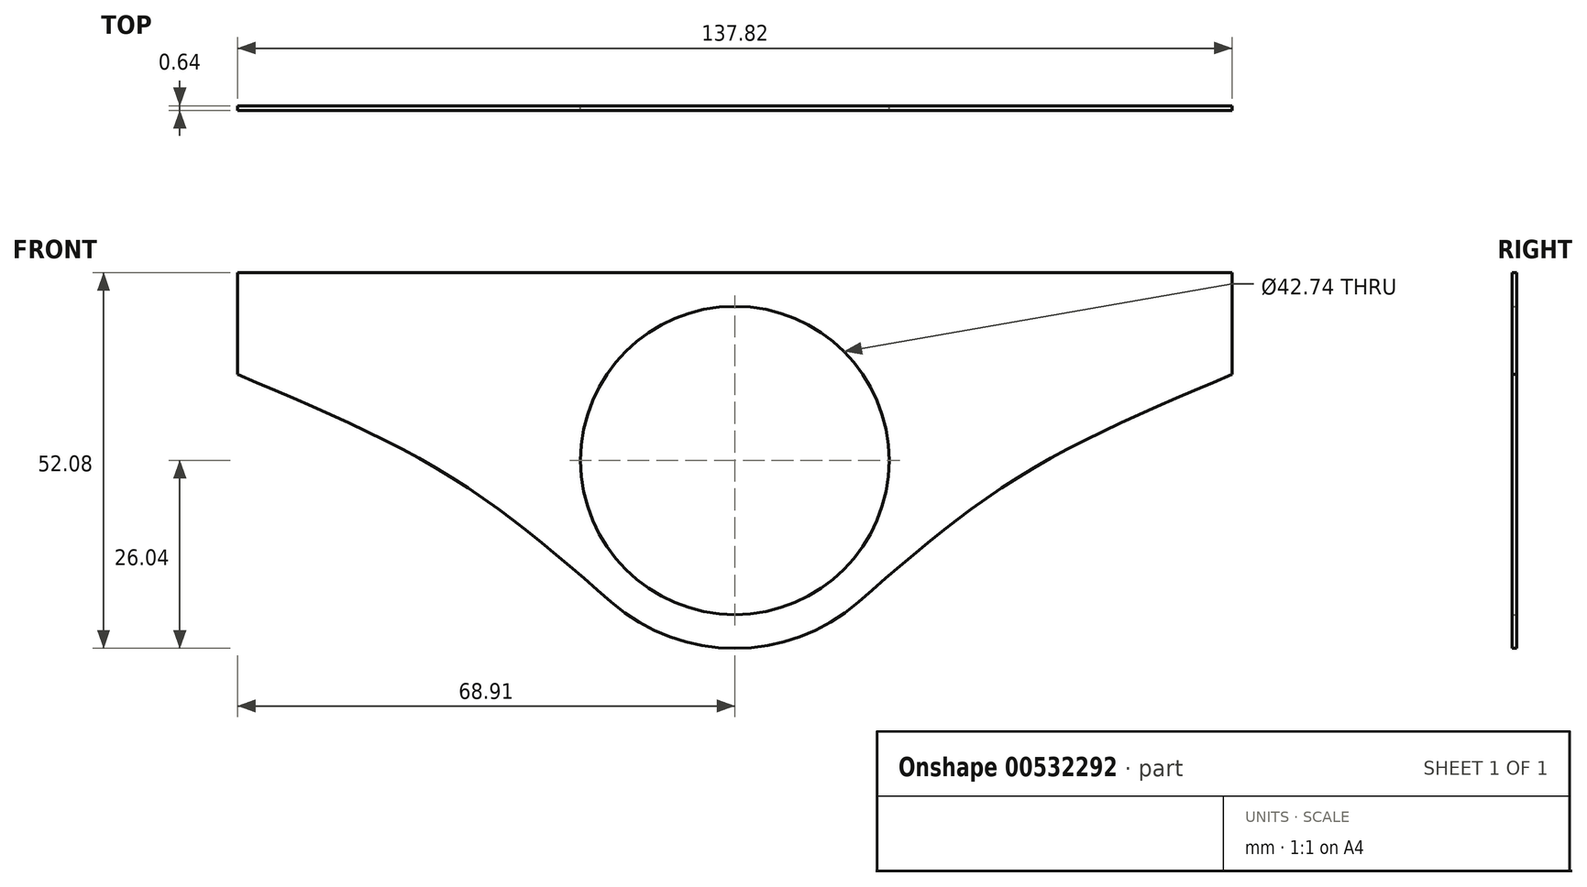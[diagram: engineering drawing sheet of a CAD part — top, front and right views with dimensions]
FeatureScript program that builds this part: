
annotation { "Feature Type Name" : "Feature", "Feature Type Description" : "" }
export const myFeature = defineFeature(function(context is Context, id is Id, definition is map)
    precondition{}
    {
        {
            var Q0;
            Q0=qCreatedBy(makeId("Front.planeOp"),FACE);
            var sketch = newSketch(context, id + "F0", { "sketchPlane" : qUnion([Q0])});
            skCircle(sketch, "E0", {"center": v(0, 0) * mm, "radius": 21.37 * mm});
            skLineSegment(sketch, "E1", {"start": v(0, 26.04) * mm, "end": v(-68.91, 26.04) * mm});
            skLineSegment(sketch, "E2", {"start": v(-68.91, 26.04) * mm, "end": v(-68.91, 11.93) * mm});
            skLineSegment(sketch, "E3.MirrorCS", {"start": v(68.91, 26.04) * mm, "end": v(68.91, 11.93) * mm});
            skLineSegment(sketch, "E4.MirrorCS", {"start": v(0, 26.04) * mm, "end": v(68.91, 26.04) * mm});
            skFitSpline(sketch, "E5", {"points": [v(-68.91, 11.93) * mm, v(-39.3, -2.3) * mm, v(-17.13, -19.61) * mm], "startDerivative": vector(59.84, -25.18) * mm, "endDerivative": vector(43.56, -38.04) * mm});
            skFitSpline(sketch, "E6.MirrorCS", {"points": [v(68.91, 11.93) * mm, v(39.3, -2.3) * mm, v(17.13, -19.61) * mm], "startDerivative": vector(-59.84, -25.18) * mm, "endDerivative": vector(-43.56, -38.04) * mm});
            skFitSpline(sketch, "E7.MirrorCS", {"points": [v(-68.91, 11.93) * mm, v(-39.3, -2.3) * mm, v(-17.13, -19.61) * mm], "startDerivative": vector(59.84, -25.18) * mm, "endDerivative": vector(43.56, -38.04) * mm});
            skArc(sketch, "E8", {"start": v(-17.13, -19.61) * mm, "mid": v(0, -26.04) * mm, "end": v(17.13, -19.61) * mm});
            skSolve(sketch);
        }
        {
            var Q0;
            Q0=makeQuery(id+"F0.imprint","IMPRINT",FACE,{"disambiguationData":[TD([[makeQuery(id+"F0.imprint","IMPRINT",EDGE,{"derivedFrom":sQuery(id+"F0.wireOp",EDGE,"E0")}),-1.0]])]});
            extrude(context, id + "F1", {"entities" : qUnion([Q0]), "depth" : 0.64 * mm, "offsetDistance" : 25.4 * mm});
        }
    });
